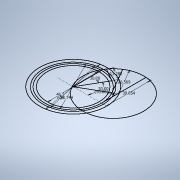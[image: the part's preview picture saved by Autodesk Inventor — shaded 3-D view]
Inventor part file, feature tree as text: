
AUTODESK INVENTOR PART (.ipt)
format: ipt  version: 2020 (Build 240168000, 168)  size: 100,864 bytes
history: native  units: in
note: dims shown in document units (in); Inventor stores cm internally (conversion verified against a paired STEP export)
features: sketch x1
ambient origin geometry x8: Origin, YZ Plane, XZ Plane, XY Plane, X Axis, Y Axis, Z Axis, Center Point
feature tree (1):
  sketch  "Sketch3"  dims[d1=1.1811in d16=1.9978in d17=30.0deg d18=30.0deg d19=0.523in d21=1.5691in d22=90.0deg d23=1.046in d24=2.126in d25=2.3622in d26=1.8307in]
